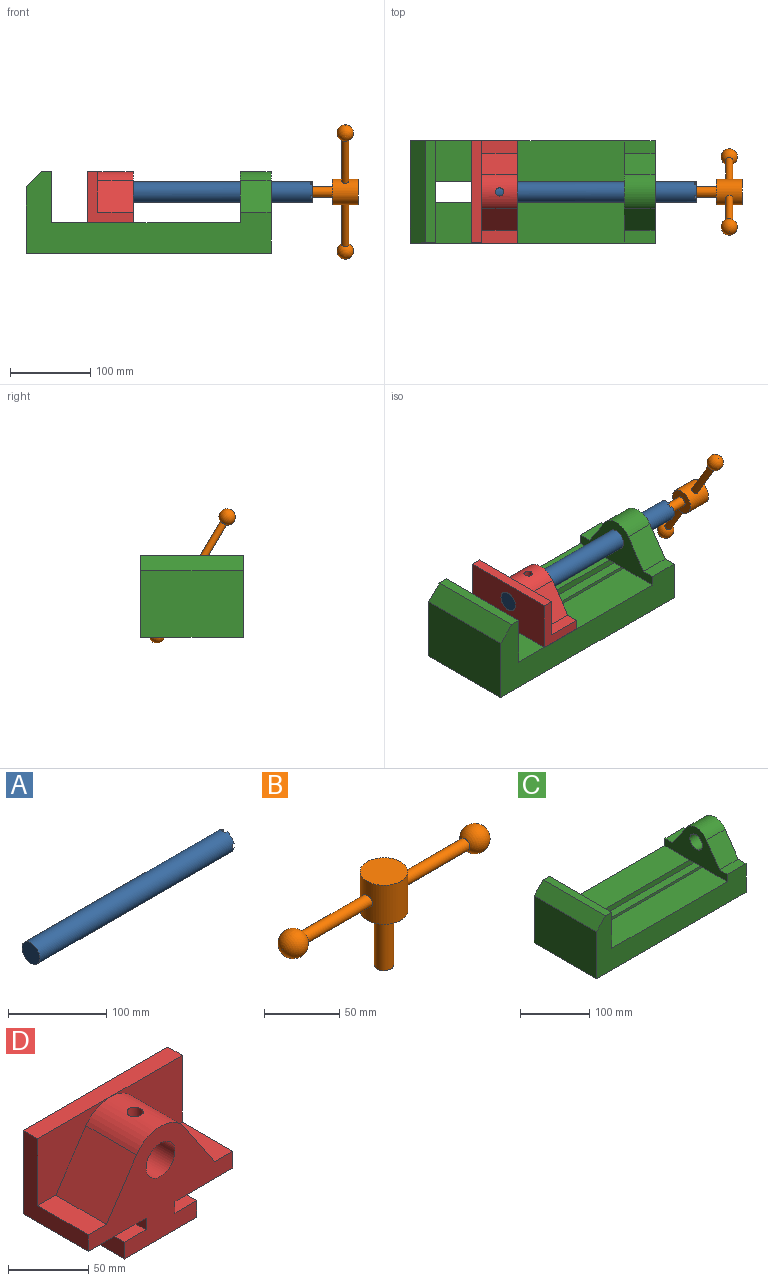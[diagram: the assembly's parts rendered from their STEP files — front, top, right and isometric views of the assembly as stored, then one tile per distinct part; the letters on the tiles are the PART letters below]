
ASSEMBLY  parts=4 mates=5
PART A: 20 faces, bbox 279.4x25.4x25.4 mm
  f0: plane 9.9x9.9mm, normal (1,0,0), area 62.3mm2, adj f3,f6,f15,f17
  f1: plane 9.9x9.9mm, normal (1,0,0), area 62.3mm2, adj f3,f6,f11,f14
  f2: plane 9.9x9.9mm, normal (1,0,0), area 62.3mm2, adj f3,f6,f8,f18
  f3: cylinder r=12.7mm len=279.4mm, axis (-1,0,0), area 22243.2mm2, adj f0,f1,f2,f4,f5,f8,f9,f10
  f4: plane 9.9x9.9mm, normal (1,0,0), area 62.3mm2, adj f3,f6,f9,f12
  f5: plane 25.4x25.4mm, normal (-1,0,0), area 506.7mm2, adj f3
  f6: cylinder r=6.35mm len=25.4mm, axis (1,0,0), area 960.3mm2, adj f0,f1,f2,f4,f7,f8,f9,f10
  f7: plane 12.7x12.7mm, normal (1,0,0), area 126.7mm2, adj f6
  f8: plane 6.62x2.54mm, normal (0,1,0), area 16.8mm2, adj f2,f3,f6,f10
  f9: plane 6.62x2.54mm, normal (0,-1,0), area 16.8mm2, adj f3,f4,f6,f10
  f10: plane 6.88x5.08mm, normal (1,0,0), area 32.7mm2, adj f3,f6,f8,f9
  f11: plane 6.62x2.54mm, normal (0,0,-1), area 16.8mm2, adj f1,f3,f6,f13
  f12: plane 6.62x2.54mm, normal (0,0,1), area 16.8mm2, adj f3,f4,f6,f13
  f13: plane 6.88x5.08mm, normal (1,0,0), area 32.7mm2, adj f3,f6,f11,f12
  f14: plane 6.62x2.54mm, normal (0,-1,0), area 16.8mm2, adj f1,f3,f6,f16
  f15: plane 6.62x2.54mm, normal (0,1,0), area 16.8mm2, adj f0,f3,f6,f16
  f16: plane 6.88x5.08mm, normal (1,0,0), area 32.7mm2, adj f3,f6,f14,f15
  f17: plane 6.62x2.54mm, normal (0,0,-1), area 16.8mm2, adj f0,f3,f6,f19
  f18: plane 6.62x2.54mm, normal (0,0,1), area 16.8mm2, adj f2,f3,f6,f19
  f19: plane 6.88x5.08mm, normal (1,0,0), area 32.7mm2, adj f3,f6,f17,f18
PART B: 9 faces, bbox 191x31.8x76.2 mm
  f0: cylinder r=15.88mm len=31.75mm, axis (0,0,-1), area 3041.4mm2, adj f1,f2,f5,f6
  f1: plane 31.75x31.75mm, normal (0,0,1), area 791.7mm2, adj f0
  f2: plane 31.75x31.75mm, normal (0,0,-1), area 665.1mm2, adj f0,f3
  f3: cylinder r=6.35mm len=44.45mm, axis (0,0,1), area 1773.5mm2, adj f2,f4
  f4: plane 12.7x12.7mm, normal (0,0,-1), area 126.7mm2, adj f3
  f5: cylinder r=4.45mm len=60.96mm, axis (-1,0,0), area 1693.6mm2, adj f0,f8
  f6: cylinder r=4.45mm len=60.96mm, axis (-1,0,0), area 1693.6mm2, adj f0,f7
  f7: sphere r=10.16mm, area 1231.8mm2, adj f6
  f8: sphere r=10.16mm, area 1231.8mm2, adj f5
PART C: 28 faces, bbox 304.8x127x101.6 mm
  f0: plane 127x101.6mm, normal (1,0,0), area 7544.8mm2, adj f7,f8,f9,f11,f12,f13,f14,f15
  f1: plane 234.95x50.8mm, normal (0,0,1), area 11935.5mm2, adj f2,f4,f9,f21
  f2: plane 127x63.5mm, normal (-1,0,0), area 4157.7mm2, adj f1,f3,f8,f9,f11,f12,f13,f14
  f3: plane 234.95x50.8mm, normal (0,0,1), area 11935.5mm2, adj f2,f4,f8,f22
  f4: plane 127x101.6mm, normal (1,0,0), area 9516.1mm2, adj f1,f3,f5,f7,f8,f9,f18,f19
  f5: plane 127x12.7mm, normal (0,0,1), area 1612.9mm2, adj f4,f8,f9,f10
  f6: plane 127x82.55mm, normal (-1,0,0), area 10483.8mm2, adj f7,f8,f9,f10
  f7: plane 304.8x127mm, normal (0,0,-1), area 31774.1mm2, adj f0,f4,f6,f8,f9,f26,f27
  f8: plane 304.8x101.6mm, normal (0,-1,0), area 13931.4mm2, adj f0,f2,f3,f4,f5,f6,f7,f10
  f9: plane 304.8x101.6mm, normal (0,1,0), area 13931.4mm2, adj f0,f1,f2,f4,f5,f6,f7,f10
  f10: plane 127x19.05mm, normal (-0.71,0,0.71), area 3421.5mm2, adj f5,f6,f8,f9
  f11: plane 38.1x15.88mm, normal (0,0,1), area 604.8mm2, adj f0,f2,f9,f13
  f12: cylinder r=25.4mm len=42.19mm, axis (1,0,0), area 1896.6mm2, adj f0,f2,f13,f15
  f13: plane 39.55x38.1mm, normal (0,0.83,0.56), area 1814.5mm2, adj f0,f2,f11,f12
  f14: plane 38.1x15.88mm, normal (0,0,1), area 604.8mm2, adj f0,f2,f8,f15
  f15: plane 39.55x38.1mm, normal (0,-0.83,0.56), area 1814.5mm2, adj f0,f2,f12,f14
  f16: cylinder r=12.7mm len=38.1mm, axis (1,0,0), area 3040.2mm2, adj f0,f2
  f17: plane 38.1x25.4mm, normal (0,0,-1), area 967.7mm2, adj f0,f2,f21,f22
  f18: plane 273.05x19.05mm, normal (0,0,1), area 5201.6mm2, adj f0,f4,f19,f26
  f19: plane 273.05x12.7mm, normal (0,-1,0), area 3467.7mm2, adj f0,f4,f18,f20
  f20: plane 273.05x19.05mm, normal (0,0,-1), area 5201.6mm2, adj f0,f4,f19,f21
  f21: plane 273.05x8.89mm, normal (0,-1,0), area 2427.4mm2, adj f0,f1,f4,f17,f20
  f22: plane 273.05x8.89mm, normal (0,1,0), area 2427.4mm2, adj f0,f3,f4,f17,f23
  f23: plane 273.05x19.05mm, normal (0,0,-1), area 5201.6mm2, adj f0,f4,f22,f24
  f24: plane 273.05x12.7mm, normal (0,1,0), area 3467.7mm2, adj f0,f4,f23,f25
  f25: plane 273.05x19.05mm, normal (0,0,1), area 5201.6mm2, adj f0,f4,f24,f27
  f26: plane 273.05x16.51mm, normal (0,-1,0), area 4508.1mm2, adj f0,f4,f7,f18
  f27: plane 273.05x16.51mm, normal (0,1,0), area 4508.1mm2, adj f0,f4,f7,f25
PART D: 23 faces, bbox 127x57.2x85.1 mm
  f0: plane 44.45x8.89mm, normal (-1,0,0), area 395.2mm2, adj f1,f7,f16,f17
  f1: plane 44.45x19.05mm, normal (0,0,1), area 846.8mm2, adj f0,f2,f16,f17
  f2: plane 44.45x12.7mm, normal (-1,0,0), area 564.5mm2, adj f1,f3,f16,f17
  f3: plane 63.5x44.45mm, normal (0,0,-1), area 2822.6mm2, adj f2,f4,f16,f17
  f4: plane 44.45x12.7mm, normal (1,0,0), area 564.5mm2, adj f3,f5,f16,f17
  f5: plane 44.45x19.05mm, normal (0,0,1), area 846.8mm2, adj f4,f6,f16,f17
  f6: plane 44.45x8.89mm, normal (1,0,0), area 395.2mm2, adj f5,f7,f16,f17
  f7: plane 127x57.15mm, normal (0,0,-1), area 6129mm2, adj f0,f6,f8,f15,f16,f17,f19
  f8: plane 63.5x57.15mm, normal (1,0,0), area 1371mm2, adj f7,f9,f16,f18,f19,f20
  f9: plane 44.45x15.88mm, normal (0,0,1), area 705.6mm2, adj f8,f10,f16,f18
  f10: plane 44.45x39.55mm, normal (0.83,0,0.56), area 2116.9mm2, adj f9,f11,f16,f18
  f11: cylinder r=25.4mm len=44.45mm, axis (0,1,0), area 2131.3mm2, adj f10,f12,f16,f18,f21,f22
  f12: plane 44.45x39.55mm, normal (-0.83,0,0.56), area 2116.9mm2, adj f11,f13,f16,f21
  f13: plane 44.45x15.88mm, normal (0,0,1), area 705.6mm2, adj f12,f15,f16,f21
  f14: cylinder r=12.7mm len=57.15mm, axis (0,1,0), area 4477.6mm2, adj f16,f19,f22
  f15: plane 63.5x57.15mm, normal (-1,0,0), area 1371mm2, adj f7,f13,f16,f19,f20,f21
  f16: plane 127x85.09mm, normal (0,-1,0), area 5190mm2, adj f0,f1,f2,f3,f4,f5,f6,f7
  f17: plane 63.5x21.59mm, normal (0,1,0), area 1032.3mm2, adj f0,f1,f2,f3,f4,f5,f6,f7
  f18: plane 63.5x50.8mm, normal (0,-1,0), area 1700mm2, adj f8,f9,f10,f11,f20
  f19: plane 127x63.5mm, normal (0,1,0), area 7557.8mm2, adj f7,f8,f14,f15,f20
  f20: plane 127x12.7mm, normal (0,0,1), area 1612.9mm2, adj f8,f15,f18,f19,f21
  f21: plane 63.5x50.8mm, normal (0,-1,0), area 1700mm2, adj f11,f12,f13,f15,f20
  f22: cylinder r=5.08mm len=13.76mm, axis (0,0,1), area 413.9mm2, adj f11,f14
PLACE A rot(axis=(1,0,0),120.7deg) t=(-43.2,24.53,33.85)mm
PLACE B rot(axis=(-0.69,0.19,-0.69),158.4deg) t=(261.44,24.53,33.85)mm
PLACE C t=(-119.68,88.03,-42.35)mm fixed
PLACE D rot(axis=(0,0,1),90deg) t=(-30.5,-38.97,-4.25)mm
MATE slider C.f4 <-> D.f17  axis (1,0,0) through (-87.93,11.83,-4.25)mm
MATE slider A.f3 <-> B.f0  axis (1,0,0) through (210.8,24.53,33.85)mm
MATE slider B.f0 <-> A.f3  axis (-1,0,0) through (216.99,24.53,33.85)mm
MATE slider A.f3 <-> B.f0  axis (1,0,0) through (210.8,24.53,33.85)mm
MATE revolute D.f11 <-> A.f3  axis (-1,0,0) through (-43.2,24.53,33.85)mm
